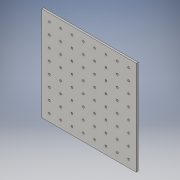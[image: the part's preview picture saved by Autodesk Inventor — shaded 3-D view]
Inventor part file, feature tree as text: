
AUTODESK INVENTOR PART (.ipt)
format: ipt  version: 2016 (Build 200138000, 138)  size: 158,208 bytes
history: native  units: in
note: dims shown in document units (in); Inventor stores cm internally (conversion verified against a paired STEP export)
features: extrude x2, sketch x2, pattern_linear x1
ambient origin geometry x8: Origin, YZ Plane, XZ Plane, XY Plane, X Axis, Y Axis, Z Axis, Center Point
bodies: Solid1 (feature_tree)
feature tree (5):
  extrude  "Extrusion1"  Depth=5.9055in
  extrude  "Extrusion2"  Depth=0.1181in
  pattern_linear  "Rectangular Pattern1"  Spacing1=0.4724in  [1 undecoded]
  sketch  "Sketch3"  dims[d0=5.9055in d1=5.9055in]
  sketch  "Sketch5"  dims[d2=0.1181in d3=0.0in d15=0.4724in d16=0.4724in d17=0.1181in d18=0.1181in d19=0.0in d20=3.1496in d22=0.7087in d23=3.1496in d25=0.7087in]
note: 1 required parameter value undecoded (feature->parameter linkage not recoverable at this tier; creation-order binding heuristic only, values carry confidence <= 0.55)
